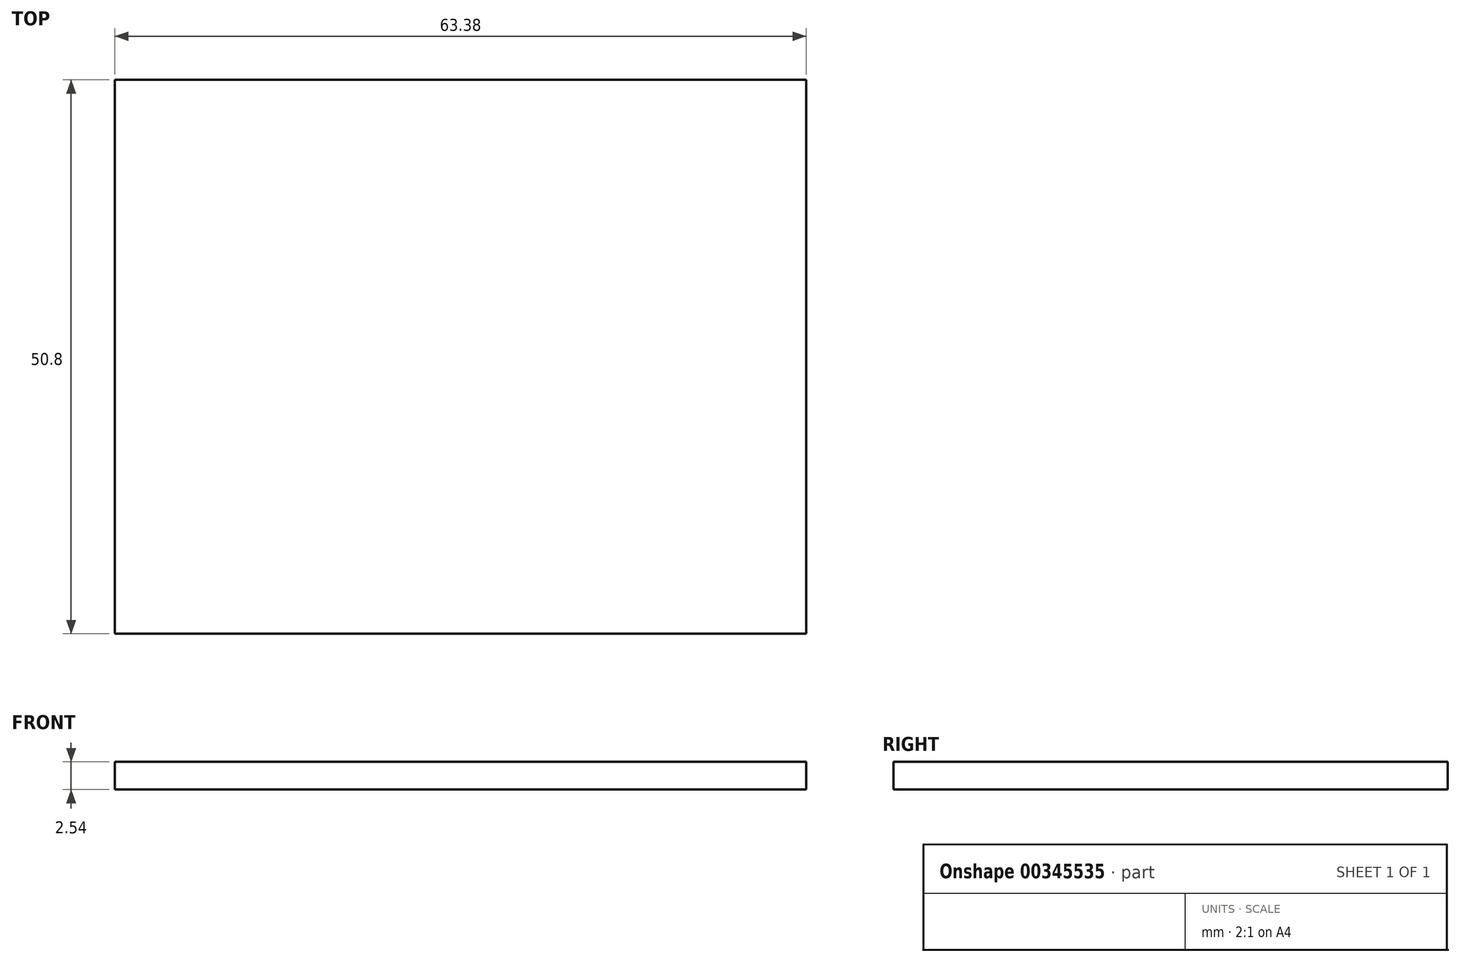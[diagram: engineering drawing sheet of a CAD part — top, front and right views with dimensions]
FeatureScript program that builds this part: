
annotation { "Feature Type Name" : "Feature", "Feature Type Description" : "" }
export const myFeature = defineFeature(function(context is Context, id is Id, definition is map)
    precondition{}
    {
        {
            var Q0;
            Q0=qCreatedBy(makeId("Top.planeOp"),FACE);
            var sketch = newSketch(context, id + "F0", { "sketchPlane" : qUnion([Q0])});
            skLineSegment(sketch, "E0.bottom", {"start": v(-31.69, -25.4) * mm, "end": v(31.69, -25.4) * mm});
            skLineSegment(sketch, "E0.top", {"start": v(-31.69, 25.4) * mm, "end": v(31.69, 25.4) * mm});
            skLineSegment(sketch, "E0.left", {"start": v(-31.69, -25.4) * mm, "end": v(-31.69, 25.4) * mm});
            skLineSegment(sketch, "E0.right", {"start": v(31.69, -25.4) * mm, "end": v(31.69, 25.4) * mm});
            skPoint(sketch, "E0.middle", {"position": v(0, 0) * mm});
            skSolve(sketch);
        }
        {
            var Q0;
            Q0 = qSketchRegion(id + "F0", true);
            extrude(context, id + "F1", {"entities" : qUnion([Q0]), "depth" : 2.54 * mm});
        }
    });
